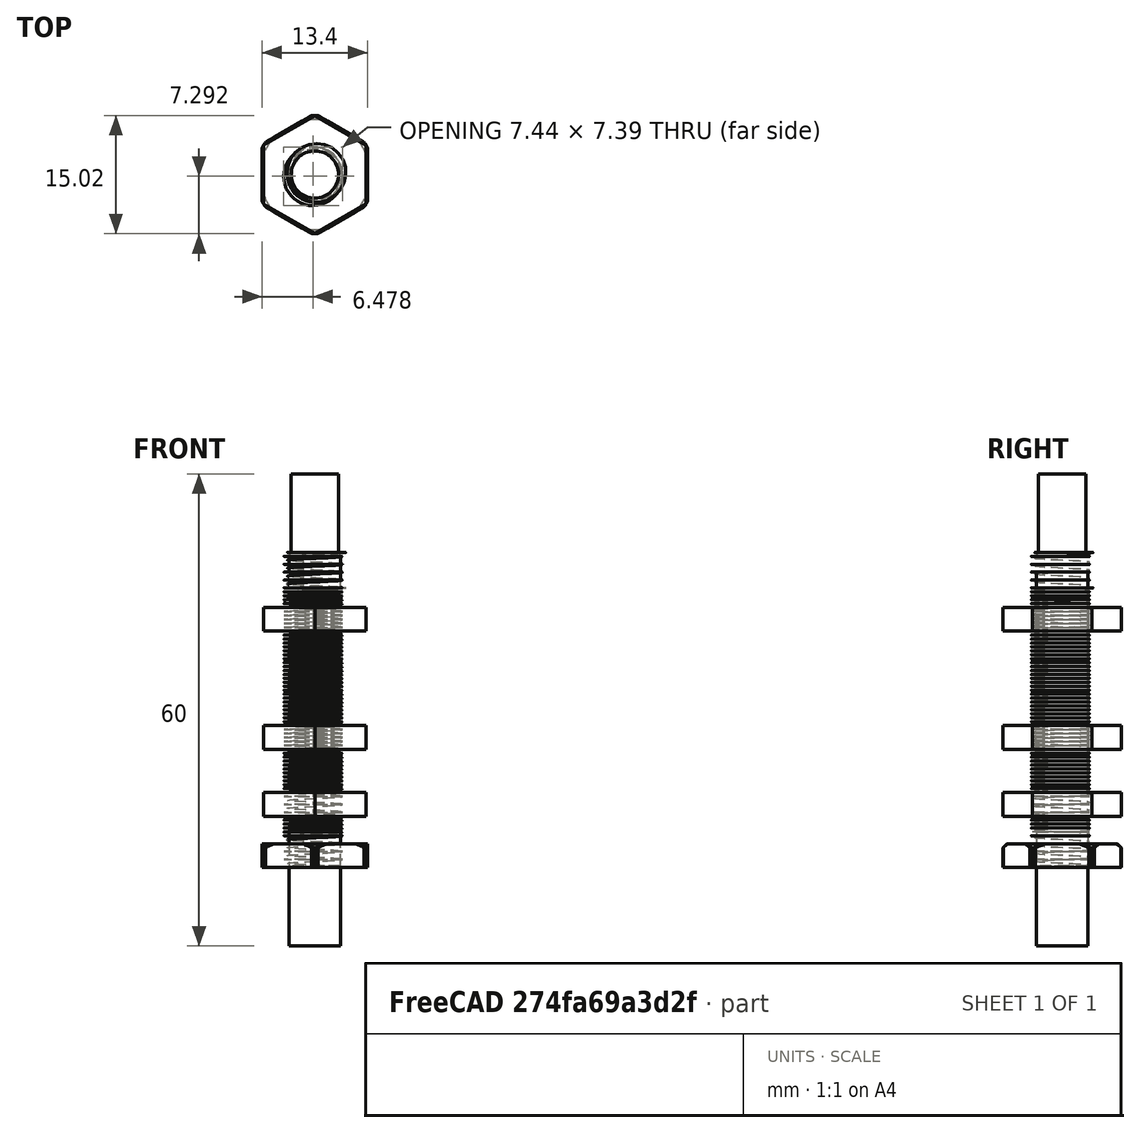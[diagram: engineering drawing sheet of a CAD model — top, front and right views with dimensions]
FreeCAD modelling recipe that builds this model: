
FCSTD DOCUMENT  (FreeCAD 0.19R24291 (Git))
Label: LJ8A3-2
License: All rights reserved
LicenseURL: http://en.wikipedia.org/wiki/All_rights_reserved
objects: Sketcher::SketchObject×9, PartDesign::Pad×8, PartDesign::Body×8, PartDesign::CoordinateSystem×6, App::Part×3, Part::Part2DObjectPython×2, Part::Helix×2, PartDesign::Chamfer×2, App::DocumentObjectGroup×2, Part::Sweep×1, Part::Extrusion×1, Part::MultiCommon×1, Part::Feature×1, Part::Refine×1, Part::MultiFuse×1, App::FeaturePython×1, PartDesign::Fillet×1, PartDesign::ShapeBinder×1, PartDesign::AdditivePipe×1
note: 58 computed .brp shape members not serialized (recipe doc carries the construction recipe); baked Part::Feature solids carry a one-line shape summary decoded from their .brp

FEATURE [Sketcher::SketchObject] Sketch
  FullyConstrained = false
  MapMode = 5
  Support = -> [XY_Plane]
  sketch-geometry (1):
    g0: Circle CenterX=0 CenterY=0 CenterZ=0 NormalX=0 NormalY=0 NormalZ=1 AngleXU=0 Radius=3.25
  constraints (2):
    c: Coincident(g0,g-1)
    c: Diameter(g0) = 6.5
FEATURE [PartDesign::Pad] Pad
  Direction = (1,1,1)
  Length = 4.5
  Length2 = 100
  Profile = -> Sketch
  Type = 0
FEATURE [Part::Part2DObjectPython] VThreadProfile  # Draft 2D object (typed FeaturePython)
  Area = 43.7265
  Closed = true
  Continuity = C3
  Instructions = Expand this with the ... button to view instructions | Sweep this object along a helix of the same pitch to produce your thread. | It is recommended to make the helix in the ThreadProfile workbench. | If there is an active Body the ThreadProfile object will be put into it.,If not it can be dragged and dropped into the body later. | If there is an active Body when the helix is made there will be made a ShapeBinder for it | For internal threads you will need to cut the Sweep object out of a cylinder, or if using Part Design sweep it as a Subtractive Pipe. | Always use Frenet mode | I have provided some presets, but it is possible there could be some errors.  Double check for mission critical applications. | Also, the tolerances might be different from what you wish to have.  I believe the internal minor diameters are all minimum and the external are all maximum.
  InternalOrExternal = 1
  MakeFace = true
  MinorDiameter = 7
  Parameterization = 1
  Pitch = 1
  Placement = pos=(0,0,4.5) rot=(0,0,1;0rad)
  Points = (719) [(3.49751,0.0305648,0),(3.49486,0.0610878,0),(3.49202,0.091569,0),(3.489,0.122008,0),(3.4858,0.152405,0),(3.48239,0.182759,0),(3.47879,0.213069,0),+712 more]
  Presets = 0
  Quality = 1
  ThreadCount = 35.5
  Version = 1.69
  external_data = [-0.00235387,-0.00461052,-0.00677828,-0.00886428,-0.0108747,-0.0128149,-0.0146895,-0.0165028,-0.0182584,-0.0199597,-0.0216095,-0.0232106,-0.0247653,-0.0262759,-0.0277444,-0.0291725,-0.0305621,-0.0319145,-0.0332313,-0.0345138,-0.0357632,+698 more]
  internal_data = [0,0,0,0,0,0,0,0,0,0,0,0,0,0,0,0,0,0,0,0,0,0,0,0,0,0,0,0,0,0,0,0,0,0,0,0,0,0,0,0,0,0,0,0,0,0,0,0,0,0,0,0,0,0,0,0,0,0,0,0,0,0,0,0,0,0,0,0,0,0,0,0,0,0,0,0,0,0,0,0,0,0,0,0,0,0,0,0,0,0,0,0,0,0,0,0,0,0,0,0,0,0,0,0,0,0,0,0,0,0,0,0,0,0,0,0,0,0,0,0,+599 more]
  preset_names = <blob: 3959 chars omitted>
  presets_data = [0,0,0,2.20878,24.1173,24.6888,0.25,0.693,0.729,0.25,0.793,0.829,0.25,0.893,0.929,0.3,1.032,1.075,0.35,1.171,1.221,0.35,1.371,1.421,0.4,1.509,1.567,0.45,1.648,1.713,0.45,1.948,2.013,0.5,2.387,2.459,0.6,2.764,2.85,0.7,3.141,3.242,0.75,3.58,+712 more]
FEATURE [Part::Helix] Helix
  Angle = 0
  AttacherType = Attacher::AttachEngine3D
  Height = 35.5
  LocalCoord = 0
  Pitch = 1
  Placement = pos=(0,0,4.5) rot=(0,0,1;0rad)
  Radius = 1
  Style = 0
  expr: Pitch = VThreadProfile.Pitch
  expr: Height = VThreadProfile.ThreadCount * VThreadProfile.Pitch
  expr: .Placement.Base.x = VThreadProfile.Placement.Base.x
  expr: .Placement.Base.y = VThreadProfile.Placement.Base.y
  expr: .Placement.Base.z = VThreadProfile.Placement.Base.z
  expr: .Placement.Rotation.Angle = VThreadProfile.Placement.Rotation.Angle
  expr: .Placement.Rotation.Axis.x = VThreadProfile.Placement.Rotation.Axis.x
  expr: .Placement.Rotation.Axis.y = VThreadProfile.Placement.Rotation.Axis.y
  expr: .Placement.Rotation.Axis.z = VThreadProfile.Placement.Rotation.Axis.z
FEATURE [Part::Sweep] Sweep
  Frenet = true
  Sections = -> [VThreadProfile]
  Solid = true
  Spine = -> Helix [Edge1,Edge2,Edge3,Edge4,Edge5,Edge6,Edge7,Edge8,Edge9,Edge10,Edge11,Edge12,Edge13,Edge14,Edge15,Edge16,Edge17,Edge18,Edge19,Edge20,Edge21,Edge22,Edge23,Edge24,Edge25,Edge26,Edge27,Edge28,Edge29,Edge30,Edge31,Edge32,Edge33,Edge34,Edge35,Edge36]
  Transition = 1
FEATURE [Sketcher::SketchObject] Sketch001
  FullyConstrained = false
  MapMode = 5
  Placement = pos=(0,0,4.5) rot=(0,0,1;0rad)
  Support = -> [Pad]
  sketch-geometry (1):
    g0: Circle CenterX=0 CenterY=0 CenterZ=0 NormalX=0 NormalY=0 NormalZ=1 AngleXU=0 Radius=3
  constraints (3):
    c: PointOnObject(g0,g-1)
    c: Diameter(g0) = 6
    c: DistanceX(g0) = 0
FEATURE [PartDesign::Pad] Pad001
  BaseFeature = -> Pad
  Direction = (1,1,1)
  Length = 45.5
  Length2 = 100
  Profile = -> Sketch001
  Type = 0
FEATURE [Sketcher::SketchObject] Sketch002
  AttachmentOffset = pos=(0,0,2) rot=(0,0,1;0rad)
  FullyConstrained = false
  MapMode = 5
  Placement = pos=(0,0,6.5) rot=(0,0,1;0rad)
  Support = -> [Pad001]
  sketch-geometry (7):
    g0: LineSegment StartX=0 StartY=7.5 StartZ=0 EndX=-6.49519 EndY=3.75 EndZ=0
    g1: LineSegment StartX=-6.49519 StartY=3.75 StartZ=0 EndX=-6.49519 EndY=-3.75 EndZ=0
    g2: LineSegment StartX=-6.49519 StartY=-3.75 StartZ=0 EndX=-9e-16 EndY=-7.5 EndZ=0
    g3: LineSegment StartX=-9e-16 StartY=-7.5 StartZ=0 EndX=6.49519 EndY=-3.75 EndZ=0
    g4: LineSegment StartX=6.49519 StartY=-3.75 StartZ=0 EndX=6.49519 EndY=3.75 EndZ=0
    g5: LineSegment StartX=6.49519 StartY=3.75 StartZ=0 EndX=0 EndY=7.5 EndZ=0
    g6: Circle CenterX=0 CenterY=0 CenterZ=0 NormalX=0 NormalY=0 NormalZ=1 AngleXU=0 Radius=7.5
  constraints (16):
    c: Coincident(g0,g1)
    c: Coincident(g1,g2)
    c: Coincident(g2,g3)
    c: Coincident(g3,g4)
    c: Coincident(g4,g5)
    c: Coincident(g5,g0)
    c: Equal(g0, g1-g5) x5
    c: PointOnObject(g0,g6)
    c: PointOnObject(g1,g6)
    c: PointOnObject(g2,g6)
    c: PointOnObject(g3,g6)
    c: PointOnObject(g4,g6)
    c: PointOnObject(g5,g6)
    c: Coincident(g6,g-1)
    c: Diameter(g6) = 15
    c: PointOnObject(g0,g-2)
FEATURE [PartDesign::Pad] Pad002
  BaseFeature = -> Pad001
  Direction = (1,1,1)
  Length = 3
  Length2 = 100
  Profile = -> Sketch002
  Type = 0
FEATURE [PartDesign::Body] Body001  label="Nut"
  Origin = -> Origin002
FEATURE [Sketcher::SketchObject] Sketch003  label="Nut Base"
  FullyConstrained = false
  MapMode = 5
  sketch-geometry (1):
    g0: Circle CenterX=0 CenterY=0 CenterZ=0 NormalX=0 NormalY=0 NormalZ=1 AngleXU=0 Radius=7.5
  constraints (2):
    c: PointOnObject(g0,g-1)
    c: Diameter(g0) = 15
FEATURE [PartDesign::Pad] Pad003
  Direction = (1,1,1)
  Length = 3
  Length2 = 100
  Profile = -> Sketch003
  Type = 0
FEATURE [Sketcher::SketchObject] Sketch005
  FullyConstrained = false
  MapMode = 5
  Placement = pos=(0,0,3) rot=(0,0,1;0rad)
  Support = -> [Pad003]
  sketch-geometry (7):
    g0: LineSegment StartX=6.55 StartY=-3.78164 StartZ=0 EndX=6.55 EndY=3.78164 EndZ=0
    g1: LineSegment StartX=6.55 StartY=3.78164 StartZ=0 EndX=-6.6773e-12 EndY=7.56329 EndZ=0
    g2: LineSegment StartX=-6.6773e-12 StartY=7.56329 StartZ=0 EndX=-6.55 EndY=3.78164 EndZ=0
    g3: LineSegment StartX=-6.55 StartY=3.78164 StartZ=0 EndX=-6.55 EndY=-3.78164 EndZ=0
    g4: LineSegment StartX=-6.55 StartY=-3.78164 StartZ=0 EndX=6.6782e-12 EndY=-7.56329 EndZ=0
    g5: LineSegment StartX=6.6782e-12 StartY=-7.56329 StartZ=0 EndX=6.55 EndY=-3.78164 EndZ=0
    g6: Circle CenterX=0 CenterY=0 CenterZ=0 NormalX=0 NormalY=0 NormalZ=1 AngleXU=0 Radius=7.56329
  constraints (16):
    c: Coincident(g0,g1)
    c: Coincident(g1,g2)
    c: Coincident(g2,g3)
    c: Coincident(g3,g4)
    c: Coincident(g4,g5)
    c: Coincident(g5,g0)
    c: Equal(g0, g1-g5) x5
    c: PointOnObject(g0,g6)
    c: PointOnObject(g1,g6)
    c: PointOnObject(g2,g6)
    c: PointOnObject(g3,g6)
    c: PointOnObject(g4,g6)
    c: PointOnObject(g5,g6)
    c: Coincident(g6,g-1)
    c: Parallel(g3,g-2)
    c: DistanceX(g3,g0) = 13.1
FEATURE [PartDesign::Chamfer] Chamfer
  Angle = 45
  Base = -> Pad003 [Face3]
  BaseFeature = -> Pad003
  ChamferType = 0
  FlipDirection = false
  Size = 0.5
  Size2 = 1
  SupportTransform = false
FEATURE [Part::Extrusion] Extrude001
  Base = -> Sketch005
  Dir = (0,0,-1)
  DirMode = 0
  FaceMakerClass = Part::FaceMakerBullseye
  LengthFwd = 3
  LengthRev = 0
  Solid = true
  Symmetric = false
FEATURE [Part::MultiCommon] Common
  Shapes = -> [Extrude001,Chamfer]
FEATURE [Part::Feature] Common001
  shape: bbox 14.36 x 15 x 3 mm, 20 faces (baked)
FEATURE [Part::Refine] Common001001
  Source = -> Common001
FEATURE [App::Part] Part
  Group = -> [Body001,Sketch003,Sketch005,Chamfer,Extrude001,Pad003,Common,Common001001,Common001]
  Origin = -> Origin001
FEATURE [PartDesign::Chamfer] Chamfer001
  Angle = 45
  Base = -> Pad002 [Face2]
  BaseFeature = -> Pad002
  ChamferType = 0
  FlipDirection = false
  Size = 0.2
  Size2 = 1
  SupportTransform = false
FEATURE [PartDesign::Body] Body
  Group = -> [Sketch,Pad,Sketch001,Pad001,Sketch002,Pad002,Chamfer001]
  Origin = -> Origin
  Tip = -> Chamfer001
FEATURE [Part::MultiFuse] Fusion
  Shapes = -> [Body,Sweep]
FEATURE [App::DocumentObjectGroup] Parts
  Group = -> [Part,Body]
FEATURE [PartDesign::CoordinateSystem] LCS_Origin
  AttacherType = Attacher::AttachEngine3D
  MapMode = 2
  Support = -> [X_Axis003]
FEATURE [App::DocumentObjectGroup] Constraints
FEATURE [App::FeaturePython] Variables  # WARN: FeaturePython — macro-defined, semantics opaque (R4)
FEATURE [PartDesign::CoordinateSystem] LCS_0
  AttacherType = Attacher::AttachEngine3D
  MapMode = 2
  Support = -> [X_Axis004]
FEATURE [PartDesign::CoordinateSystem] LCS_0001
  AttacherType = Attacher::AttachEngine3D
  MapMode = 2
  Support = -> [X_Axis005]
FEATURE [PartDesign::Body] ChamferBody
  Origin = -> Origin006
FEATURE [Sketcher::SketchObject] Sketch006
  AttachmentOffset = pos=(0,0,35.5) rot=(0,0,1;0rad)
  FullyConstrained = true
  MapMode = 5
  Placement = pos=(0,0,35.5) rot=(0,0,1;0rad)
  Support = -> [XY_Plane005]
  sketch-geometry (1):
    g0: Circle CenterX=0 CenterY=0 CenterZ=0 NormalX=0 NormalY=0 NormalZ=1 AngleXU=0 Radius=3.25
  constraints (2):
    c: Coincident(g0,g-1)
    c: Diameter(g0) = 6.5
FEATURE [PartDesign::Pad] Pad004
  Direction = (1,1,1)
  Length = 4.5
  Length2 = 100
  Profile = -> Sketch006
  Type = 0
FEATURE [PartDesign::Fillet] Fillet
  Base = -> Pad004 [Edge3]
  BaseFeature = -> Pad004
  Radius = 0.5
  SupportTransform = false
FEATURE [PartDesign::Body] Body_2  label="Tip"
  Group = -> [LCS_0001,Sketch006,Pad004,Fillet]
  Origin = -> Origin005
  Tip = -> Fillet
FEATURE [Part::Part2DObjectPython] VThreadProfile001  # Draft 2D object (typed FeaturePython)
  Area = 43.7265
  Closed = true
  Continuity = C3
  Instructions = Expand this with the ... button to view instructions | Sweep this object along a helix of the same pitch to produce your thread. | It is recommended to make the helix in the ThreadProfile workbench. | If there is an active Body the ThreadProfile object will be put into it.,If not it can be dragged and dropped into the body later. | If there is an active Body when the helix is made there will be made a ShapeBinder for it | For internal threads you will need to cut the Sweep object out of a cylinder, or if using Part Design sweep it as a Subtractive Pipe. | Always use Frenet mode | I have provided some presets, but it is possible there could be some errors.  Double check for mission critical applications. | Also, the tolerances might be different from what you wish to have.  I believe the internal minor diameters are all minimum and the external are all maximum.
  InternalOrExternal = 1
  MakeFace = true
  MinorDiameter = 7
  Parameterization = 1
  Pitch = 1
  Points = (719) [(3.49751,0.0305648,0),(3.49486,0.0610878,0),(3.49202,0.091569,0),(3.489,0.122008,0),(3.4858,0.152405,0),(3.48239,0.182759,0),(3.47879,0.213069,0),+712 more]
  Presets = 0
  Quality = 1
  ThreadCount = 35.5
  Version = 1.69
  external_data = [-0.00235387,-0.00461052,-0.00677828,-0.00886428,-0.0108747,-0.0128149,-0.0146895,-0.0165028,-0.0182584,-0.0199597,-0.0216095,-0.0232106,-0.0247653,-0.0262759,-0.0277444,-0.0291725,-0.0305621,-0.0319145,-0.0332313,-0.0345138,-0.0357632,+698 more]
  internal_data = [0,0,0,0,0,0,0,0,0,0,0,0,0,0,0,0,0,0,0,0,0,0,0,0,0,0,0,0,0,0,0,0,0,0,0,0,0,0,0,0,0,0,0,0,0,0,0,0,0,0,0,0,0,0,0,0,0,0,0,0,0,0,0,0,0,0,0,0,0,0,0,0,0,0,0,0,0,0,0,0,0,0,0,0,0,0,0,0,0,0,0,0,0,0,0,0,0,0,0,0,0,0,0,0,0,0,0,0,0,0,0,0,0,0,0,0,0,0,0,0,+599 more]
  preset_names = <blob: 3959 chars omitted>
  presets_data = [0,0,0,2.20878,24.1173,24.6888,0.25,0.693,0.729,0.25,0.793,0.829,0.25,0.893,0.929,0.3,1.032,1.075,0.35,1.171,1.221,0.35,1.371,1.421,0.4,1.509,1.567,0.45,1.648,1.713,0.45,1.948,2.013,0.5,2.387,2.459,0.6,2.764,2.85,0.7,3.141,3.242,0.75,3.58,+712 more]
FEATURE [Part::Helix] Helix001
  Angle = 0
  AttacherType = Attacher::AttachEngine3D
  Height = 35.5
  LocalCoord = 0
  Pitch = 1
  Radius = 4
  Style = 0
  expr: .Placement.Rotation.Axis.z = VThreadProfile001.Placement.Rotation.Axis.z
  expr: .Placement.Rotation.Axis.y = VThreadProfile001.Placement.Rotation.Axis.y
  expr: .Placement.Rotation.Axis.x = VThreadProfile001.Placement.Rotation.Axis.x
  expr: .Placement.Rotation.Angle = VThreadProfile001.Placement.Rotation.Angle
  expr: .Placement.Base.z = VThreadProfile001.Placement.Base.z
  expr: .Placement.Base.y = VThreadProfile001.Placement.Base.y
  expr: .Placement.Base.x = VThreadProfile001.Placement.Base.x
  expr: Height = VThreadProfile001.ThreadCount * VThreadProfile001.Pitch
  expr: Pitch = VThreadProfile001.Pitch
FEATURE [PartDesign::ShapeBinder] ShapeBinder
  Support = -> [Helix001]
  TraceSupport = false
FEATURE [PartDesign::AdditivePipe] AdditivePipe
  AuxilleryCurvelinear = true
  AuxillerySpineTangent = false
  Binormal = (0,0,0)
  Mode = 2
  Profile = -> VThreadProfile001
  Spine = -> ShapeBinder
  SpineTangent = false
  Transformation = 0
  Transition = 0
FEATURE [PartDesign::Body] Body002  label="M8 Body"
  Group = -> [VThreadProfile001,ShapeBinder,AdditivePipe]
  Origin = -> Origin007
  Tip = -> AdditivePipe
FEATURE [PartDesign::CoordinateSystem] LCS_0002
  AttacherType = Attacher::AttachEngine3D
  MapMode = 2
  Support = -> [X_Axis008]
FEATURE [Sketcher::SketchObject] Sketch007
  FullyConstrained = true
  MapMode = 5
  Support = -> [XY_Plane008]
  sketch-geometry (1):
    g0: Circle CenterX=0 CenterY=0 CenterZ=0 NormalX=0 NormalY=0 NormalZ=1 AngleXU=0 Radius=3.25
  constraints (2):
    c: Coincident(g0,g-1)
    c: Diameter(g0) = 6.5
FEATURE [PartDesign::Pad] Pad005
  Direction = (1,1,1)
  Length = 10
  Length2 = 100
  Profile = -> Sketch007
  Reversed = true
  Type = 0
FEATURE [PartDesign::Body] LED_indicator
  Group = -> [LCS_0002,Sketch007,Pad005]
  Origin = -> Origin008
  Tip = -> Pad005
FEATURE [PartDesign::CoordinateSystem] LCS_0003
  AttacherType = Attacher::AttachEngine3D
  MapMode = 2
  Support = -> [X_Axis009]
FEATURE [Sketcher::SketchObject] Sketch008
  AttachmentOffset = pos=(0,0,30) rot=(0,0,1;0rad)
  FullyConstrained = true
  MapMode = 5
  Placement = pos=(0,0,30) rot=(0,0,1;0rad)
  Support = -> [XY_Plane009]
  sketch-geometry (7):
    g0: LineSegment StartX=6.5 StartY=-3.75278 StartZ=0 EndX=6.5 EndY=3.75278 EndZ=0
    g1: LineSegment StartX=6.5 StartY=3.75278 StartZ=0 EndX=-9e-16 EndY=7.50555 EndZ=0
    g2: LineSegment StartX=-9e-16 StartY=7.50555 StartZ=0 EndX=-6.5 EndY=3.75278 EndZ=0
    g3: LineSegment StartX=-6.5 StartY=3.75278 StartZ=0 EndX=-6.5 EndY=-3.75278 EndZ=0
    g4: LineSegment StartX=-6.5 StartY=-3.75278 StartZ=0 EndX=0 EndY=-7.50555 EndZ=0
    g5: LineSegment StartX=0 StartY=-7.50555 StartZ=0 EndX=6.5 EndY=-3.75278 EndZ=0
    g6: Circle CenterX=0 CenterY=0 CenterZ=0 NormalX=0 NormalY=0 NormalZ=1 AngleXU=0 Radius=7.50555
  constraints (16):
    c: Coincident(g0,g1)
    c: Coincident(g1,g2)
    c: Coincident(g2,g3)
    c: Coincident(g3,g4)
    c: Coincident(g4,g5)
    c: Coincident(g5,g0)
    c: Equal(g0, g1-g5) x5
    c: PointOnObject(g0,g6)
    c: PointOnObject(g1,g6)
    c: PointOnObject(g2,g6)
    c: PointOnObject(g3,g6)
    c: PointOnObject(g4,g6)
    c: PointOnObject(g5,g6)
    c: Coincident(g6,g-1)
    c: Parallel(g0,g-2)
    c: DistanceX(g3,g0) = 13
FEATURE [PartDesign::Pad] Pad006
  Direction = (1,1,1)
  Length = 3
  Length2 = 100
  Profile = -> Sketch008
  Type = 0
FEATURE [PartDesign::Body] Top_Nut
  Group = -> [LCS_0003,Sketch008,Pad006]
  Origin = -> Origin009
  Tip = -> Pad006
FEATURE [PartDesign::CoordinateSystem] LCS_0004
  AttacherType = Attacher::AttachEngine3D
  MapMode = 2
  Support = -> [X_Axis010]
FEATURE [Sketcher::SketchObject] Sketch009
  AttachmentOffset = pos=(0,0,15) rot=(0,0,1;0rad)
  FullyConstrained = true
  MapMode = 5
  Placement = pos=(0,0,15) rot=(0,0,1;0rad)
  Support = -> [XY_Plane010]
  sketch-geometry (7):
    g0: LineSegment StartX=6.5 StartY=3.75278 StartZ=0 EndX=9e-16 EndY=7.50555 EndZ=0
    g1: LineSegment StartX=9e-16 StartY=7.50555 StartZ=0 EndX=-6.5 EndY=3.75278 EndZ=0
    g2: LineSegment StartX=-6.5 StartY=3.75278 StartZ=0 EndX=-6.5 EndY=-3.75278 EndZ=0
    g3: LineSegment StartX=-6.5 StartY=-3.75278 StartZ=0 EndX=0 EndY=-7.50555 EndZ=0
    g4: LineSegment StartX=0 StartY=-7.50555 StartZ=0 EndX=6.5 EndY=-3.75278 EndZ=0
    g5: LineSegment StartX=6.5 StartY=-3.75278 StartZ=0 EndX=6.5 EndY=3.75278 EndZ=0
    g6: Circle CenterX=0 CenterY=0 CenterZ=0 NormalX=0 NormalY=0 NormalZ=1 AngleXU=0 Radius=7.50555
  constraints (16):
    c: Coincident(g0,g1)
    c: Coincident(g1,g2)
    c: Coincident(g2,g3)
    c: Coincident(g3,g4)
    c: Coincident(g4,g5)
    c: Coincident(g5,g0)
    c: Equal(g0, g1-g5) x5
    c: PointOnObject(g0,g6)
    c: PointOnObject(g1,g6)
    c: PointOnObject(g2,g6)
    c: PointOnObject(g3,g6)
    c: PointOnObject(g4,g6)
    c: PointOnObject(g5,g6)
    c: Coincident(g6,g-1)
    c: Parallel(g5,g-2)
    c: DistanceX(g2,g4) = 13
FEATURE [PartDesign::Pad] Pad007
  Direction = (1,1,1)
  Length = 3
  Length2 = 100
  Profile = -> Sketch009
  Type = 0
FEATURE [PartDesign::Body] Bottom_Nit  label="Bottom_Nut"
  Group = -> [LCS_0004,Sketch009,Pad007]
  Origin = -> Origin010
  Tip = -> Pad007
FEATURE [App::Part] Tip  label="Sensor"
  Group = -> [LCS_0,Body_2,Body002,Helix001,LED_indicator,Top_Nut,Bottom_Nit]
  Origin = -> Origin004
FEATURE [App::Part] Model
  Configuration = 0
  Group = -> [LCS_Origin,Constraints,Variables,Tip]
  Origin = -> Origin003
  Type = Assembly4 Model
